# Revit family: Gira_031400
name_source: partatom
category: Allgemeines Modell
revit_build: Autodesk Revit 2017 (Build: 20160225_1515(x64)
units: mm (PartAtom-declared; Revit-internal decimal feet)

## family parameters
Basisbauteil = Fläche
Beim Laden mit Abzugskörper schneiden = Nein
Bemaßung runder Anschluss = Durchmesser verwenden
Gemeinsam genutzt = Nein
Kann Basisbauteil für Bewehrung sein = Nein
Raumberechnungspunkt = Nein
Teiletyp = Normal

## types (1)
- Gira_031400
    App control via Bluetooth = Nein
    Applicable with button = Ja
    Applicable with infrared button = Nein
    Applicable with movement sensor = Nein
    Applicable with presence indicator = Nein
    Applicable with time switch/timer = Nein
    Applicable with transmission button = Nein
    Assembly arrangement = Basic element
    BIM = https://media.stage.bim.site
    Basic element without cover = Ja
    Beschreibung = Speed reg.rot o o 0.1-2.7A Ins.,Speed regulator insert with rotary on off switch,,0,1 -2.7 A,Features:,- Speed regulator for speed control of single-phase motors such as induction motors, shaded-pole motors, and universal motors.,- Excess-temperature protection, manual restarting after cool-down.,- Switching output for slat control or for switching ohmic loads.,- With spring plug terminals.
    Colour = Other
    Connection type = Plug clamp
    Data sheet = https://katalog.gira.de
    Degree of protection (IP) = IP20
    Dimming phase cut-off = Nein
    Dimming phase cut-on = Nein
    Frequency [Hz] = [50:60]
    Function lighting = Illuminated (on)
    GTIN = 4010337314004
    HAN = 031400
    Halogen free = Nein
    Hersteller = Gira
    Illumination = None
    Imprint = None
    Label space/information surface = Nein
    Label space/information surface 1 = No
    Label space/information surface 2 = No
    Label space/information surface 3 = No
    Light value memory = Nein
    Material = Other
    Material quality = Other
    Method of operation = Turn button
    Model = Single push button
    Mounting method = Flush mounted (plaster)
    Nominal voltage [Volt] = 250
    Nominal voltage [Volt] 1 = [230:230]
    Number of modules (module system) = 1
    Number of phases = 1
    Number of rockers = 2
    Power control step less = Ja
    Productwebsite = http://katalog.gira.de
    Push button switch = Nein
    Rated current = 10 A
    Serial dimmer = Nein
    Substation input = Nein
    Suitable for degree of protection (IP) = IP20
    Surface protection = Other
    Transparent = Nein
    Type of fastening = Mounting with claw and screw
    Type of lighting = Glow lamp
    Type of load = Other
    Typname = Speed regul. rot.on/off 0.1 - 2.7 A Insert
    URL = https://www.gira.de
    Vorgabe-Ansicht = 1219 mm
    Washing machine switch = Nein
    Wiring system = Series switch
    With lighting = Nein
    With mounting plate = Nein
    With temperature sensor = Nein

## geometry (parser evidence)
native form markers: Sweep x2
no freeform markers — native parametric forms only
